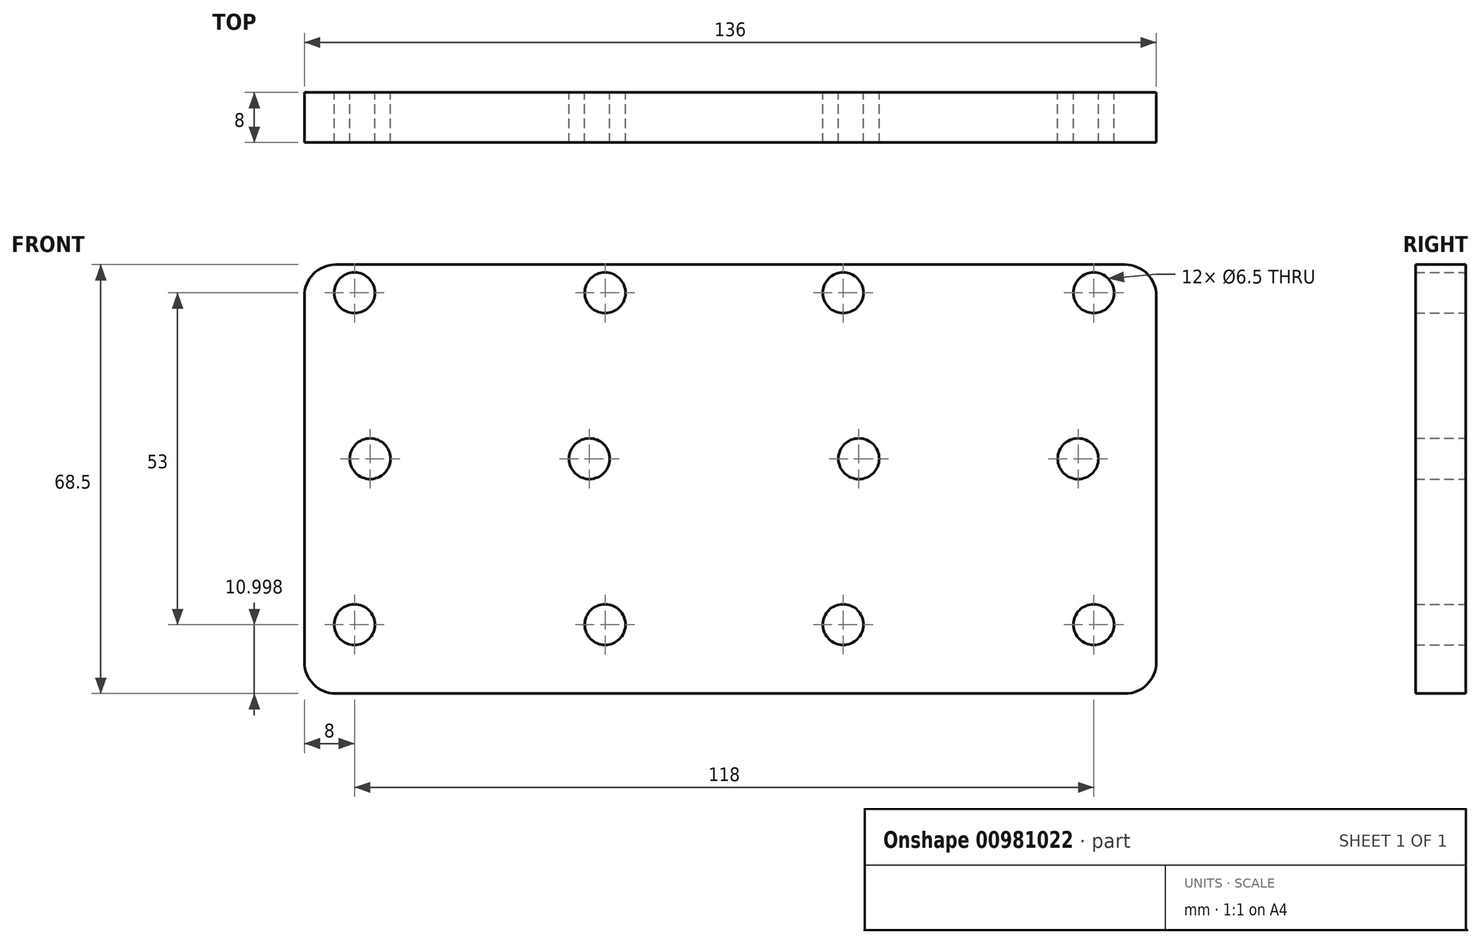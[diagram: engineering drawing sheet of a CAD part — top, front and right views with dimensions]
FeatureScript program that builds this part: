
annotation { "Feature Type Name" : "Feature", "Feature Type Description" : "" }
export const myFeature = defineFeature(function(context is Context, id is Id, definition is map)
    precondition{}
    {
        {
            var Q0;
            Q0=qCreatedBy(makeId("Front.planeOp"),FACE);
            var sketch = newSketch(context, id + "F0", { "sketchPlane" : qUnion([Q0])});
            skLineSegment(sketch, "E0", {"start": v(75, -81.84) * mm, "end": v(-51, -81.84) * mm});
            skLineSegment(sketch, "E1", {"start": v(-56, -76.84) * mm, "end": v(-56, -18.34) * mm});
            skCircle(sketch, "E2", {"center": v(70, -70.84) * mm, "radius": 3.25 * mm});
            skCircle(sketch, "E3", {"center": v(70, -17.84) * mm, "radius": 3.25 * mm});
            skCircle(sketch, "E4", {"center": v(30, -17.84) * mm, "radius": 3.25 * mm});
            skCircle(sketch, "E5", {"center": v(30, -70.84) * mm, "radius": 3.25 * mm});
            skCircle(sketch, "E6", {"center": v(32.5, -44.34) * mm, "radius": 3.25 * mm});
            skCircle(sketch, "E7", {"center": v(67.5, -44.34) * mm, "radius": 3.25 * mm});
            skCircle(sketch, "E8.MirrorC", {"center": v(-8, -17.84) * mm, "radius": 3.25 * mm});
            skCircle(sketch, "E9.MirrorC", {"center": v(-48, -17.84) * mm, "radius": 3.25 * mm});
            skCircle(sketch, "E10.MirrorC", {"center": v(-45.5, -44.34) * mm, "radius": 3.25 * mm});
            skCircle(sketch, "E11.MirrorC", {"center": v(-10.5, -44.34) * mm, "radius": 3.25 * mm});
            skCircle(sketch, "E12.MirrorC", {"center": v(-8, -70.84) * mm, "radius": 3.25 * mm});
            skCircle(sketch, "E13.MirrorC", {"center": v(-48, -70.84) * mm, "radius": 3.25 * mm});
            skPoint(sketch, "E14.visualSharp", {"position": v(-56, -80.84) * mm});
            skArc(sketch, "E14.filletArc", {"start": v(-56, -76.84) * mm, "mid": v(-54.54, -80.38) * mm, "end": v(-51, -81.84) * mm});
            skPoint(sketch, "E15.visualSharp", {"position": v(80, -80.84) * mm});
            skArc(sketch, "E15.filletArc", {"start": v(75, -81.84) * mm, "mid": v(78.54, -80.38) * mm, "end": v(80, -76.84) * mm});
            skLineSegment(sketch, "E16", {"start": v(80, -18.34) * mm, "end": v(80, -76.84) * mm});
            skLineSegment(sketch, "E17", {"start": v(-51, -13.34) * mm, "end": v(75, -13.34) * mm});
            skPoint(sketch, "E18.visualSharp", {"position": v(-56, -13.34) * mm});
            skArc(sketch, "E18.filletArc", {"start": v(-51, -13.34) * mm, "mid": v(-54.54, -14.8) * mm, "end": v(-56, -18.34) * mm});
            skPoint(sketch, "E19.visualSharp", {"position": v(80, -13.34) * mm});
            skArc(sketch, "E19.filletArc", {"start": v(80, -18.34) * mm, "mid": v(78.54, -14.8) * mm, "end": v(75, -13.34) * mm});
            skSolve(sketch);
        }
        {
            var Q0;
            Q0=qSketchRegion(id+"F0",true);
            extrude(context, id + "F1", {"entities" : qUnion([Q0]), "depth" : 8 * mm, "offsetDistance" : 25 * mm});
        }
    });
